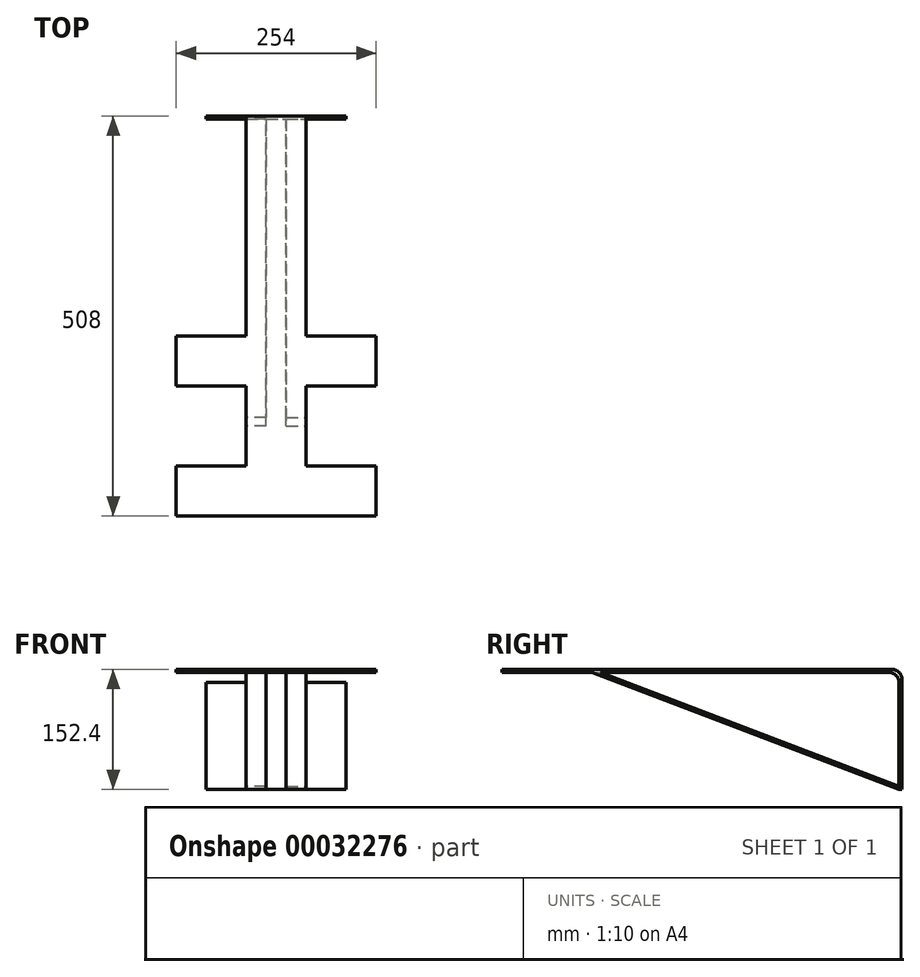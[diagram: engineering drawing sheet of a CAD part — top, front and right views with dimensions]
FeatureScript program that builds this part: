
annotation { "Feature Type Name" : "Feature", "Feature Type Description" : "" }
export const myFeature = defineFeature(function(context is Context, id is Id, definition is map)
    precondition{}
    {
        {
            var Q0;
            Q0=qCreatedBy(makeId("Top.planeOp"),FACE);
            var sketch = newSketch(context, id + "F0", { "sketchPlane" : qUnion([Q0])});
            skLineSegment(sketch, "E0", {"start": v(165.1, -508) * mm, "end": v(165.1, -444.5) * mm});
            skLineSegment(sketch, "E1", {"start": v(165.1, -444.5) * mm, "end": v(76.2, -444.5) * mm});
            skLineSegment(sketch, "E2", {"start": v(76.2, -444.5) * mm, "end": v(76.2, -342.9) * mm});
            skLineSegment(sketch, "E3", {"start": v(76.2, -342.9) * mm, "end": v(165.1, -342.9) * mm});
            skLineSegment(sketch, "E4", {"start": v(165.1, -342.9) * mm, "end": v(165.1, -279.4) * mm});
            skLineSegment(sketch, "E5", {"start": v(165.1, -279.4) * mm, "end": v(76.2, -279.4) * mm});
            skLineSegment(sketch, "E6", {"start": v(76.2, -279.4) * mm, "end": v(76.2, 0) * mm});
            skLineSegment(sketch, "E7", {"start": v(76.2, 0) * mm, "end": v(0, 0) * mm});
            skLineSegment(sketch, "E8", {"start": v(0, 0) * mm, "end": v(0, -279.4) * mm});
            skLineSegment(sketch, "E9", {"start": v(0, -279.4) * mm, "end": v(-88.9, -279.4) * mm});
            skLineSegment(sketch, "E10", {"start": v(-88.9, -279.4) * mm, "end": v(-88.9, -342.9) * mm});
            skLineSegment(sketch, "E11", {"start": v(-88.9, -342.9) * mm, "end": v(0, -342.9) * mm});
            skLineSegment(sketch, "E12", {"start": v(0, -342.9) * mm, "end": v(0, -444.5) * mm});
            skLineSegment(sketch, "E13", {"start": v(0, -444.5) * mm, "end": v(-88.9, -444.5) * mm});
            skLineSegment(sketch, "E14", {"start": v(-88.9, -444.5) * mm, "end": v(-88.9, -508) * mm});
            skLineSegment(sketch, "E15", {"start": v(-88.9, -508) * mm, "end": v(165.1, -508) * mm});
            skSolve(sketch);
        }
        {
            var Q0;
            Q0=makeQuery(id+"F0.imprint","IMPRINT",FACE,{"disambiguationData":[TD([[makeQuery(id+"F0.imprint","IMPRINT",EDGE,{"derivedFrom":sQuery(id+"F0.wireOp",EDGE,"E0")}),1.0]])]});
            extrude(context, id + "F1", {"entities" : qUnion([Q0]), "depth" : 152.4 * mm});
        }
        {
            var Q0;
            Q0=makeQuery(id+"F1.opExtrude","SWEPT_FACE",FACE,{"disambiguationData":[OSD([sQuery(id+"F0.wireOp",EDGE,"E15")])]});
            var sketch = newSketch(context, id + "F2", { "sketchPlane" : qUnion([Q0])});
            skLineSegment(sketch, "E16.bottom", {"start": v(-88.9, 0) * mm, "end": v(165.1, 0) * mm});
            skLineSegment(sketch, "E16.top", {"start": v(-88.9, 148.6) * mm, "end": v(165.1, 148.6) * mm});
            skLineSegment(sketch, "E16.left", {"start": v(-88.9, 0) * mm, "end": v(-88.9, 148.6) * mm});
            skLineSegment(sketch, "E16.right", {"start": v(165.1, 0) * mm, "end": v(165.1, 148.6) * mm});
            skSolve(sketch);
        }
        {
            var Q0;
            Q0=makeQuery(id+"F2.imprint","IMPRINT",FACE,{"disambiguationData":[TD([[makeQuery(id+"F2.imprint","IMPRINT",EDGE,{"derivedFrom":sQuery(id+"F2.wireOp",EDGE,"E16.bottom")}),1.0]])]});
            extrude(context, id + "F3", {"entities" : qUnion([Q0]), "operationType" : NewBodyOperationType.REMOVE, "oppositeDirection" : true, "depth" : 504.2 * mm});
        }
        {
            var Q0;
            Q0=makeQuery(id+"F1.opExtrude","CAP_EDGE",EDGE,{"disambiguationData":[OSD([sQuery(id+"F0.wireOp",EDGE,"E7")])],"isStart":false});
            var Q1;
            Q1=makeQuery(id+"F3.boolean.opBoolean","COPY",EDGE,{"derivedFrom":makeQuery(id+"F3.opExtrude","CAP_EDGE",EDGE,{"disambiguationData":[OSD([sQuery(id+"F2.wireOp",EDGE,"E16.top")])],"isStart":false})});
            fillet(context, id + "F4", {"entities" : qUnion([Q0, Q1]), "radius" : 12.7 * mm, "tangentPropagation" : true, "allowEdgeOverflow" : false});
        }
        {
            var Q0;
            Q0=makeQuery(id+"F1.opExtrude","SWEPT_FACE",FACE,{"disambiguationData":[OSD([sQuery(id+"F0.wireOp",EDGE,"E6")])]});
            var sketch = newSketch(context, id + "F5", { "sketchPlane" : qUnion([Q0])});
            skLineSegment(sketch, "E17.bottom", {"start": v(0, 0) * mm, "end": v(-3.81, 0) * mm});
            skLineSegment(sketch, "E17.top", {"start": v(0, 135.9) * mm, "end": v(-3.81, 135.9) * mm});
            skLineSegment(sketch, "E17.left", {"start": v(0, 0) * mm, "end": v(0, 135.9) * mm});
            skLineSegment(sketch, "E17.right", {"start": v(-3.81, 0) * mm, "end": v(-3.81, 135.9) * mm});
            skSolve(sketch);
        }
        {
            var Q0;
            Q0 = qSketchRegion(id + "F5", true);
            extrude(context, id + "F6", {"entities" : qUnion([Q0]), "operationType" : NewBodyOperationType.ADD, "depth" : 50.8 * mm});
        }
        {
            var Q0;
            Q0=makeQuery(id+"F1.opExtrude","SWEPT_FACE",FACE,{"disambiguationData":[OSD([sQuery(id+"F0.wireOp",EDGE,"E8")])]});
            var sketch = newSketch(context, id + "F7", { "sketchPlane" : qUnion([Q0])});
            skLineSegment(sketch, "E18.bottom", {"start": v(0, 0) * mm, "end": v(3.81, 0) * mm});
            skLineSegment(sketch, "E18.top", {"start": v(0, 135.9) * mm, "end": v(3.81, 135.9) * mm});
            skLineSegment(sketch, "E18.left", {"start": v(0, 0) * mm, "end": v(0, 135.9) * mm});
            skLineSegment(sketch, "E18.right", {"start": v(3.81, 0) * mm, "end": v(3.81, 135.9) * mm});
            skSolve(sketch);
        }
        {
            var Q0;
            Q0=makeQuery(id+"F7.imprint","IMPRINT",FACE,{"disambiguationData":[TD([[makeQuery(id+"F7.imprint","IMPRINT",EDGE,{"derivedFrom":sQuery(id+"F7.wireOp",EDGE,"E18.bottom")}),1.0]])]});
            extrude(context, id + "F8", {"entities" : qUnion([Q0]), "operationType" : NewBodyOperationType.ADD, "depth" : 50.8 * mm});
        }
        {
            var Q0;
            Q0=makeQuery(id+"F1.opExtrude","SWEPT_FACE",FACE,{"disambiguationData":[OSD([sQuery(id+"F0.wireOp",EDGE,"E6")])]});
            var sketch = newSketch(context, id + "F9", { "sketchPlane" : qUnion([Q0])});
            skLineSegment(sketch, "E19", {"start": v(-3.81, 0) * mm, "end": v(-393.7, 148.59) * mm});
            skLineSegment(sketch, "E20", {"start": v(-393.7, 148.6) * mm, "end": v(-383, 148.6) * mm});
            skLineSegment(sketch, "E21", {"start": v(-383, 148.6) * mm, "end": v(-3.8, 4.08) * mm});
            skLineSegment(sketch, "E22", {"start": v(-3.8, 4.08) * mm, "end": v(-3.8, 0) * mm});
            skSolve(sketch);
        }
        {
            var Q0;
            Q0=makeQuery(id+"F9.imprint","IMPRINT",FACE,{"disambiguationData":[TD([[makeQuery(id+"F9.imprint","IMPRINT",EDGE,{"derivedFrom":sQuery(id+"F9.wireOp",EDGE,"E19")}),-1.0]])]});
            extrude(context, id + "F10", {"entities" : qUnion([Q0]), "operationType" : NewBodyOperationType.ADD, "oppositeDirection" : true, "depth" : 25.4 * mm});
        }
        {
            var Q0;
            Q0=makeQuery(id+"F1.opExtrude","SWEPT_FACE",FACE,{"disambiguationData":[OSD([sQuery(id+"F0.wireOp",EDGE,"E12")])]});
            var sketch = newSketch(context, id + "F11", { "sketchPlane" : qUnion([Q0])});
            skLineSegment(sketch, "E23", {"start": v(393.7, 148.6) * mm, "end": v(3.8, 0) * mm});
            skLineSegment(sketch, "E24", {"start": v(3.81, 0) * mm, "end": v(3.81, 4.08) * mm});
            skLineSegment(sketch, "E25", {"start": v(3.8, 4.08) * mm, "end": v(383, 148.6) * mm});
            skLineSegment(sketch, "E26", {"start": v(383, 148.6) * mm, "end": v(393.7, 148.6) * mm});
            skSolve(sketch);
        }
        {
            var Q0;
            Q0 = qSketchRegion(id + "F11", true);
            extrude(context, id + "F12", {"entities" : qUnion([Q0]), "operationType" : NewBodyOperationType.ADD, "oppositeDirection" : true, "depth" : 25.4 * mm});
        }
    });
